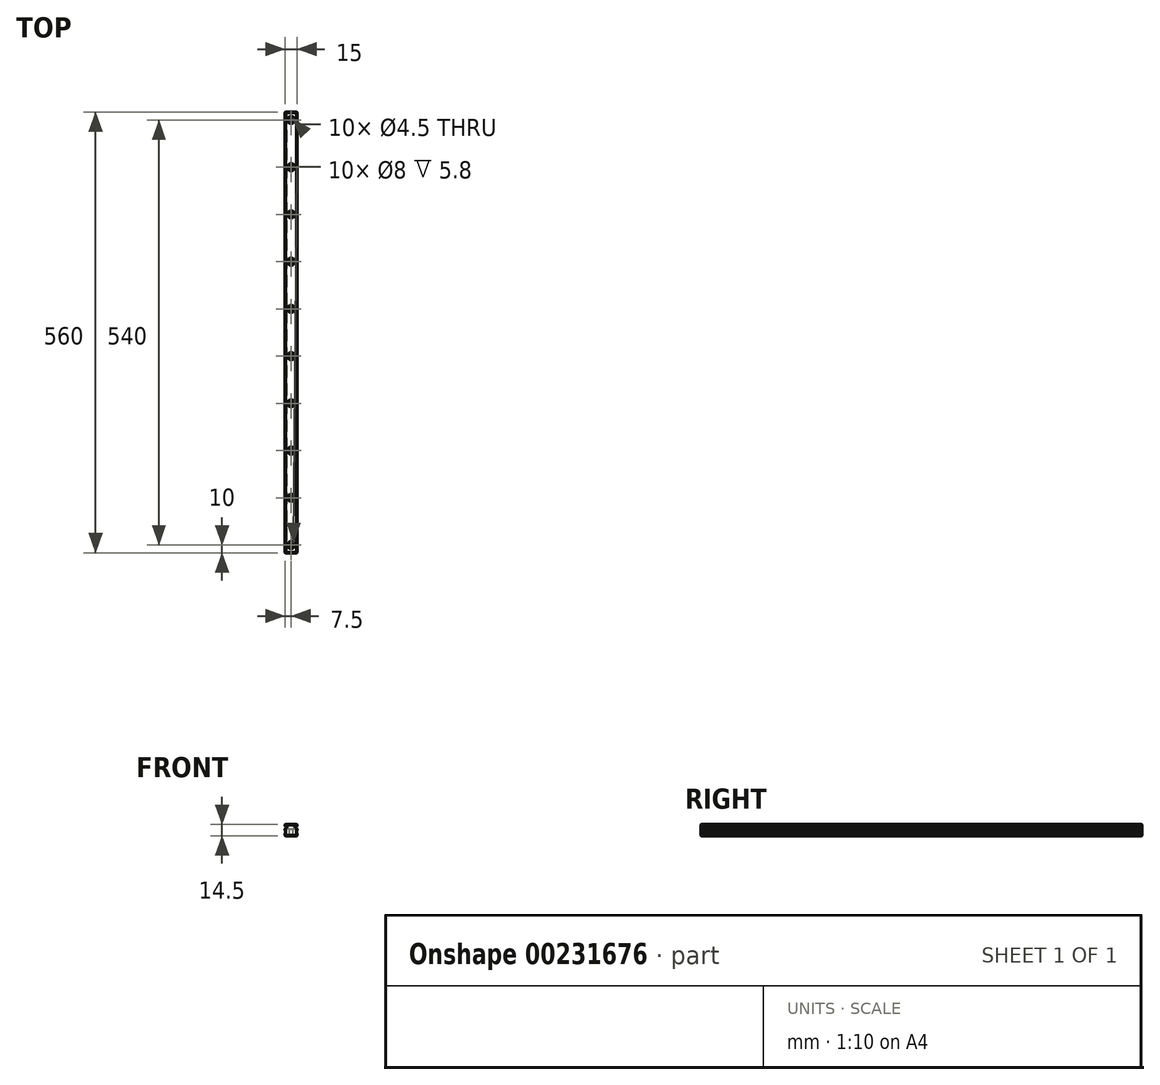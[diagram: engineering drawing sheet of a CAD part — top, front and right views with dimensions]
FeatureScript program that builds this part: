
annotation { "Feature Type Name" : "Feature", "Feature Type Description" : "" }
export const myFeature = defineFeature(function(context is Context, id is Id, definition is map)
    precondition{}
    {
        {
            var Q0;
            Q0=qCreatedBy(makeId("Front.planeOp"),FACE);
            var sketch = newSketch(context, id + "F0", { "sketchPlane" : qUnion([Q0])});
            skLineSegment(sketch, "E0", {"start": v(0, 7.25) * mm, "end": v(0, -7.25) * mm, "construction": true});
            skLineSegment(sketch, "E1", {"start": v(0, -7.25) * mm, "end": v(-7.5, -7.25) * mm});
            skLineSegment(sketch, "E2", {"start": v(-7.5, -7.25) * mm, "end": v(-7.5, -4.13) * mm});
            skLineSegment(sketch, "E3", {"start": v(-7.5, -4.13) * mm, "end": v(-7.5, -4.13) * mm});
            skLineSegment(sketch, "E4", {"start": v(-6.8, -3.43) * mm, "end": v(-6.8, -0.7) * mm});
            skLineSegment(sketch, "E5", {"start": v(-7.5, 0) * mm, "end": v(-7.5, 0) * mm});
            skLineSegment(sketch, "E6", {"start": v(-7.5, 0) * mm, "end": v(-7.5, 1.88) * mm});
            skLineSegment(sketch, "E7", {"start": v(-7.5, 1.88) * mm, "end": v(-7.5, 1.88) * mm});
            skLineSegment(sketch, "E8", {"start": v(-6.8, 2.88) * mm, "end": v(-5.5, 2.88) * mm});
            skLineSegment(sketch, "E9", {"start": v(-5.5, 2.88) * mm, "end": v(-5.5, 4.38) * mm});
            skLineSegment(sketch, "E10", {"start": v(-5.5, 4.38) * mm, "end": v(-6.8, 4.38) * mm});
            skLineSegment(sketch, "E11", {"start": v(-6.8, 4.38) * mm, "end": v(-6.8, 4.68) * mm});
            skLineSegment(sketch, "E12", {"start": v(-7.5, 5.38) * mm, "end": v(-7.5, 5.38) * mm});
            skLineSegment(sketch, "E13", {"start": v(-7.5, 5.38) * mm, "end": v(-7.5, 7.25) * mm});
            skLineSegment(sketch, "E14", {"start": v(-7.5, 7.25) * mm, "end": v(0, 7.25) * mm});
            skLineSegment(sketch, "E15", {"start": v(-6.8, 2.58) * mm, "end": v(-6.8, 2.87) * mm});
            skPoint(sketch, "E16.visualSharp", {"position": v(-6.8, -4.13) * mm});
            skArc(sketch, "E16.filletArc", {"start": v(-7.5, -4.13) * mm, "mid": v(-7, -3.92) * mm, "end": v(-6.8, -3.43) * mm});
            skPoint(sketch, "E17.visualSharp", {"position": v(-6.8, 0) * mm});
            skArc(sketch, "E17.filletArc", {"start": v(-6.8, -0.7) * mm, "mid": v(-7, -0.2) * mm, "end": v(-7.5, 0) * mm});
            skPoint(sketch, "E18.visualSharp", {"position": v(-6.8, 1.88) * mm});
            skArc(sketch, "E18.filletArc", {"start": v(-7.5, 1.88) * mm, "mid": v(-7, 2.08) * mm, "end": v(-6.8, 2.58) * mm});
            skPoint(sketch, "E19.visualSharp", {"position": v(-6.8, 5.38) * mm});
            skArc(sketch, "E19.filletArc", {"start": v(-6.8, 4.68) * mm, "mid": v(-7, 5.17) * mm, "end": v(-7.5, 5.38) * mm});
            skLineSegment(sketch, "E20.MirrorCS", {"start": v(6.8, 2.58) * mm, "end": v(6.8, 2.87) * mm});
            skLineSegment(sketch, "E21.MirrorCS", {"start": v(6.8, 4.38) * mm, "end": v(6.8, 4.68) * mm});
            skArc(sketch, "E22.MirrorCS", {"start": v(6.8, 4.68) * mm, "mid": v(7, 5.17) * mm, "end": v(7.5, 5.38) * mm});
            skArc(sketch, "E23.MirrorCS", {"start": v(7.5, 1.88) * mm, "mid": v(7, 2.08) * mm, "end": v(6.8, 2.58) * mm});
            skArc(sketch, "E24.MirrorCS", {"start": v(7.5, -4.13) * mm, "mid": v(7, -3.92) * mm, "end": v(6.8, -3.43) * mm});
            skArc(sketch, "E25.MirrorCS", {"start": v(6.8, -0.7) * mm, "mid": v(7, -0.2) * mm, "end": v(7.5, 0) * mm});
            skLineSegment(sketch, "E26.MirrorCS", {"start": v(7.5, 0) * mm, "end": v(7.5, 0) * mm});
            skLineSegment(sketch, "E27.MirrorCS", {"start": v(7.5, -7.25) * mm, "end": v(7.5, -4.13) * mm});
            skPoint(sketch, "E28.MirrorP", {"position": v(6.8, 0) * mm});
            skPoint(sketch, "E29.MirrorP", {"position": v(6.8, 5.38) * mm});
            skPoint(sketch, "E30.MirrorP", {"position": v(6.8, 1.88) * mm});
            skLineSegment(sketch, "E31.MirrorCS", {"start": v(7.5, -4.13) * mm, "end": v(7.5, -4.13) * mm});
            skLineSegment(sketch, "E32.MirrorCS", {"start": v(7.5, 1.88) * mm, "end": v(7.5, 1.88) * mm});
            skLineSegment(sketch, "E33.MirrorCS", {"start": v(7.5, 5.38) * mm, "end": v(7.5, 5.38) * mm});
            skLineSegment(sketch, "E34.MirrorCS", {"start": v(7.5, 5.38) * mm, "end": v(7.5, 7.25) * mm});
            skLineSegment(sketch, "E35.MirrorCS", {"start": v(5.5, 4.38) * mm, "end": v(6.8, 4.38) * mm});
            skLineSegment(sketch, "E36.MirrorCS", {"start": v(6.8, -3.43) * mm, "end": v(6.8, -0.7) * mm});
            skPoint(sketch, "E37.MirrorP", {"position": v(6.8, -4.13) * mm});
            skLineSegment(sketch, "E38.MirrorCS", {"start": v(6.8, 2.88) * mm, "end": v(5.5, 2.88) * mm});
            skLineSegment(sketch, "E39.MirrorCS", {"start": v(7.5, 0) * mm, "end": v(7.5, 1.88) * mm});
            skLineSegment(sketch, "E40.MirrorCS", {"start": v(5.5, 2.88) * mm, "end": v(5.5, 4.38) * mm});
            skLineSegment(sketch, "E41.MirrorCS", {"start": v(7.5, 7.25) * mm, "end": v(0, 7.25) * mm});
            skLineSegment(sketch, "E42.MirrorCS", {"start": v(0, -7.25) * mm, "end": v(7.5, -7.25) * mm});
            skSolve(sketch);
        }
        {
            var Q0;
            Q0 = qSketchRegion(id + "F0", true);
            extrude(context, id + "F1", {"entities" : qUnion([Q0]), "oppositeDirection" : true, "depth" : 560 * mm});
        }
        {
            var Q0;
            Q0=makeQuery(id+"F1.opExtrude","SWEPT_FACE",FACE,{"disambiguationData":[OSD([sQuery(id+"F0.wireOp",EDGE,"E14"),sQuery(id+"F0.wireOp",EDGE,"E41.MirrorCS")])]});
            var sketch = newSketch(context, id + "F2", { "sketchPlane" : qUnion([Q0])});
            skLineSegment(sketch, "E43", {"start": v(0, 0) * mm, "end": v(0, 560) * mm, "construction": true});
            skCircle(sketch, "E44", {"center": v(0, 10) * mm, "radius": 2.25 * mm});
            skCircle(sketch, "E45", {"center": v(0, 70) * mm, "radius": 2.25 * mm});
            skCircle(sketch, "E46", {"center": v(0, 130) * mm, "radius": 2.25 * mm});
            skCircle(sketch, "E47", {"center": v(0, 190) * mm, "radius": 2.25 * mm});
            skCircle(sketch, "E48", {"center": v(0, 250) * mm, "radius": 2.25 * mm});
            skCircle(sketch, "E49", {"center": v(0, 310) * mm, "radius": 2.25 * mm});
            skCircle(sketch, "E50", {"center": v(0, 370) * mm, "radius": 2.25 * mm});
            skCircle(sketch, "E51", {"center": v(0, 430) * mm, "radius": 2.25 * mm});
            skCircle(sketch, "E52", {"center": v(0, 490) * mm, "radius": 2.25 * mm});
            skCircle(sketch, "E53", {"center": v(0, 550) * mm, "radius": 2.25 * mm});
            skSolve(sketch);
        }
        {
            var Q0;
            Q0 = qSketchRegion(id + "F2", true);
            extrude(context, id + "F3", {"entities" : qUnion([Q0]), "operationType" : NewBodyOperationType.REMOVE, "endBound" : BoundingType.UP_TO_NEXT, "oppositeDirection" : true, "depth" : 25 * mm});
        }
        {
            var Q0;
            Q0=makeQuery(id+"F1.opExtrude","SWEPT_FACE",FACE,{"disambiguationData":[OSD([sQuery(id+"F0.wireOp",EDGE,"E14"),sQuery(id+"F0.wireOp",EDGE,"E41.MirrorCS")])]});
            var sketch = newSketch(context, id + "F4", { "sketchPlane" : qUnion([Q0])});
            skCircle(sketch, "E54", {"center": v(0, 10) * mm, "radius": 4 * mm});
            skCircle(sketch, "E55", {"center": v(0, 70) * mm, "radius": 4 * mm});
            skCircle(sketch, "E56", {"center": v(0, 130) * mm, "radius": 4 * mm});
            skCircle(sketch, "E57", {"center": v(0, 190) * mm, "radius": 4 * mm});
            skCircle(sketch, "E58", {"center": v(0, 250) * mm, "radius": 4 * mm});
            skCircle(sketch, "E59", {"center": v(0, 310) * mm, "radius": 4 * mm});
            skCircle(sketch, "E60", {"center": v(0, 370) * mm, "radius": 4 * mm});
            skCircle(sketch, "E61", {"center": v(0, 430) * mm, "radius": 4 * mm});
            skCircle(sketch, "E62", {"center": v(0, 490) * mm, "radius": 4 * mm});
            skCircle(sketch, "E63", {"center": v(0, 550) * mm, "radius": 4 * mm});
            skSolve(sketch);
        }
        {
            var Q0;
            Q0 = qSketchRegion(id + "F4", true);
            extrude(context, id + "F5", {"entities" : qUnion([Q0]), "operationType" : NewBodyOperationType.REMOVE, "oppositeDirection" : true, "depth" : 6.3 * mm});
        }
        {
            var Q0;
            Q0=makeQuery(id+"F1.opExtrude","SWEPT_FACE",FACE,{"disambiguationData":[OSD([sQuery(id+"F0.wireOp",EDGE,"E14"),sQuery(id+"F0.wireOp",EDGE,"E41.MirrorCS")])]});
            var Q1;
            Q1=makeQuery(id+"F1.opExtrude","SWEPT_FACE",FACE,{"disambiguationData":[OSD([sQuery(id+"F0.wireOp",EDGE,"E1"),sQuery(id+"F0.wireOp",EDGE,"E42.MirrorCS")])]});
            var Q2;
            Q2=makeQuery(id+"F1.opExtrude","CAP_EDGE",EDGE,{"disambiguationData":[OSD([sQuery(id+"F0.wireOp",EDGE,"E13")])],"isStart":true});
            var Q3;
            Q3=makeQuery(id+"F1.opExtrude","CAP_EDGE",EDGE,{"disambiguationData":[OSD([sQuery(id+"F0.wireOp",EDGE,"E6")])],"isStart":true});
            var Q4;
            Q4=makeQuery(id+"F1.opExtrude","CAP_EDGE",EDGE,{"disambiguationData":[OSD([sQuery(id+"F0.wireOp",EDGE,"E2")])],"isStart":true});
            var Q5;
            Q5=makeQuery(id+"F1.opExtrude","CAP_EDGE",EDGE,{"disambiguationData":[OSD([sQuery(id+"F0.wireOp",EDGE,"E27.MirrorCS")])],"isStart":true});
            var Q6;
            Q6=makeQuery(id+"F1.opExtrude","CAP_EDGE",EDGE,{"disambiguationData":[OSD([sQuery(id+"F0.wireOp",EDGE,"E39.MirrorCS")])],"isStart":true});
            var Q7;
            Q7=makeQuery(id+"F1.opExtrude","CAP_EDGE",EDGE,{"disambiguationData":[OSD([sQuery(id+"F0.wireOp",EDGE,"E34.MirrorCS")])],"isStart":true});
            var Q8;
            Q8=makeQuery(id+"F1.opExtrude","CAP_EDGE",EDGE,{"disambiguationData":[OSD([sQuery(id+"F0.wireOp",EDGE,"E2")])],"isStart":false});
            var Q9;
            Q9=makeQuery(id+"F1.opExtrude","CAP_EDGE",EDGE,{"disambiguationData":[OSD([sQuery(id+"F0.wireOp",EDGE,"E6")])],"isStart":false});
            var Q10;
            Q10=makeQuery(id+"F1.opExtrude","CAP_EDGE",EDGE,{"disambiguationData":[OSD([sQuery(id+"F0.wireOp",EDGE,"E13")])],"isStart":false});
            var Q11;
            Q11=makeQuery(id+"F1.opExtrude","CAP_EDGE",EDGE,{"disambiguationData":[OSD([sQuery(id+"F0.wireOp",EDGE,"E34.MirrorCS")])],"isStart":false});
            var Q12;
            Q12=makeQuery(id+"F1.opExtrude","CAP_EDGE",EDGE,{"disambiguationData":[OSD([sQuery(id+"F0.wireOp",EDGE,"E39.MirrorCS")])],"isStart":false});
            var Q13;
            Q13=makeQuery(id+"F1.opExtrude","CAP_EDGE",EDGE,{"disambiguationData":[OSD([sQuery(id+"F0.wireOp",EDGE,"E27.MirrorCS")])],"isStart":false});
            chamfer(context, id + "F6", {"entities" : qUnion([Q0, Q1, Q2, Q3, Q4, Q5, Q6, Q7, Q8, Q9, Q10, Q11, Q12, Q13]), "width" : 0.5 * mm, "tangentPropagation" : true});
        }
    });
